# Revit family: Basin-Wall_Hung-Sloan-SS-3003_Series
name_source: partatom
category: Plumbing Fixtures
revit_build: Autodesk Revit 2014 (Build: 20130308_1515(x64)
units: mm (PartAtom-declared; Revit-internal decimal feet)

## types (5) — shared parameters
ADA Compliant = Yes
Assembly Code = D2010310
CW Connection = Yes
CWFU = 1.5
Cold Water Connection Diameter = 3/8"
Cold Water Connection Height = 11"
Cold Water Connection Radius = 3/16"
Cold Water Connection Width = 4"
Default Elevation = 34"
HW Connection = Yes
HWFU = 1.5
Height = 34"
Hot Water Connection Diameter = 0"
Hot Water Connection Height = 11"
Hot Water Connection Radius = 3/16"
Hot Water Connection Width = 4"
Length = 18 1/4"
Manufacturer = Sloan Valve Company
Material = Vitreous China-Sloan-White
Product Documentation Link = https://specifications.sloan.com
Product URL = https://www.sloan.com
Revised Date = 8/10/2015
URL = http://www.sloan.com
Vent Connection = No
WFU = 2
Waste Connection = Yes
Waste Connection Diameter = 1 1/4"
Waste Connection Height = 12 3/4"
Waste Connection Radius = 5/8"
Width = 20 3/4"

## per-type parameters (varying)
| type | Description | Hole Distance | Hole Visibility | Model | Order Code |
| SS-3003 | Complete vitreous china lavatory with backsplash. Standard Wall Hung Lavatory with Backsplash | 4" | Yes | SS-3003 | 3873003 |
| SS-3003-STG | 20"x18" WH Backsplash Lav-4" CS w/ SloanTec Glaze | 4" | Yes | SS-3003-STG | 3873073 |
| SS-3103 | Complete vitreous china lavatory with backsplash. Standard Wall Hung Lavatory with Backsplash | 30" | No | SS-3103 | 3873103 |
| SS-3103-STG | 20"x18" WH Backsplash Lav- Single Hole CS w/ SloanTec Glaze | 30" | No | SS-3003-STG | 3873173 |
| SS-3803 | Complete vitreous china lavatory with backsplash. Standard Wall Hung Lavatory with Backsplash | 8" | Yes | SS-3003 | 3873803 |

## geometry (parser evidence)
native form markers: Sweep x3
no freeform markers — native parametric forms only
